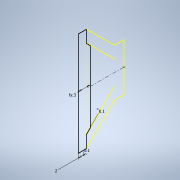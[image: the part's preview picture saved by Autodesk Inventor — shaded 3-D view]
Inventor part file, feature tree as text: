
AUTODESK INVENTOR PART (.ipt)
format: ipt  version: 2022 (Build 260153000, 153)  size: 146,432 bytes
history: native  units: mm
features: extrude x3, sketch x3, reference x3, plane x2, projected_geometry x2, other x2, mirror x1
ambient origin geometry x8: Origin, YZ Plane, XZ Plane, XY Plane, X Axis, Y Axis, Z Axis, Center Point
bodies: Solid1 (feature_tree)
feature tree (16):
  plane  "Work Plane1"
  extrude  "Extrusion1"  Depth=0.1mm
  sketch  "Sketch2"  dims[d2=2.0mm d3=3.0mm]
  plane  "Work Plane2"
  extrude  "Extrusion2"  Depth=3.0mm
  mirror  "Mirror1"
  extrude  "Extrusion3"  Depth=10.0mm TaperAngle=0.0deg
  sketch  "Sketch1"  dims[d0=0.1mm d1=0.1mm]
  reference  "Reference1"
  reference  "Reference2"
  reference  "Reference3"
  projected_geometry  "Projected Loop1"
  sketch  "Sketch3"  dims[d4=2.0mm d5=0.0mm d6=10.0mm d7=0.0mm d8=2.7mm d9=0.0mm d10=0.0mm]
  projected_geometry  "Projected Loop2"
  other  "Solids Feeder Head Assembly.iam"
  other  "solids hopper:1"
